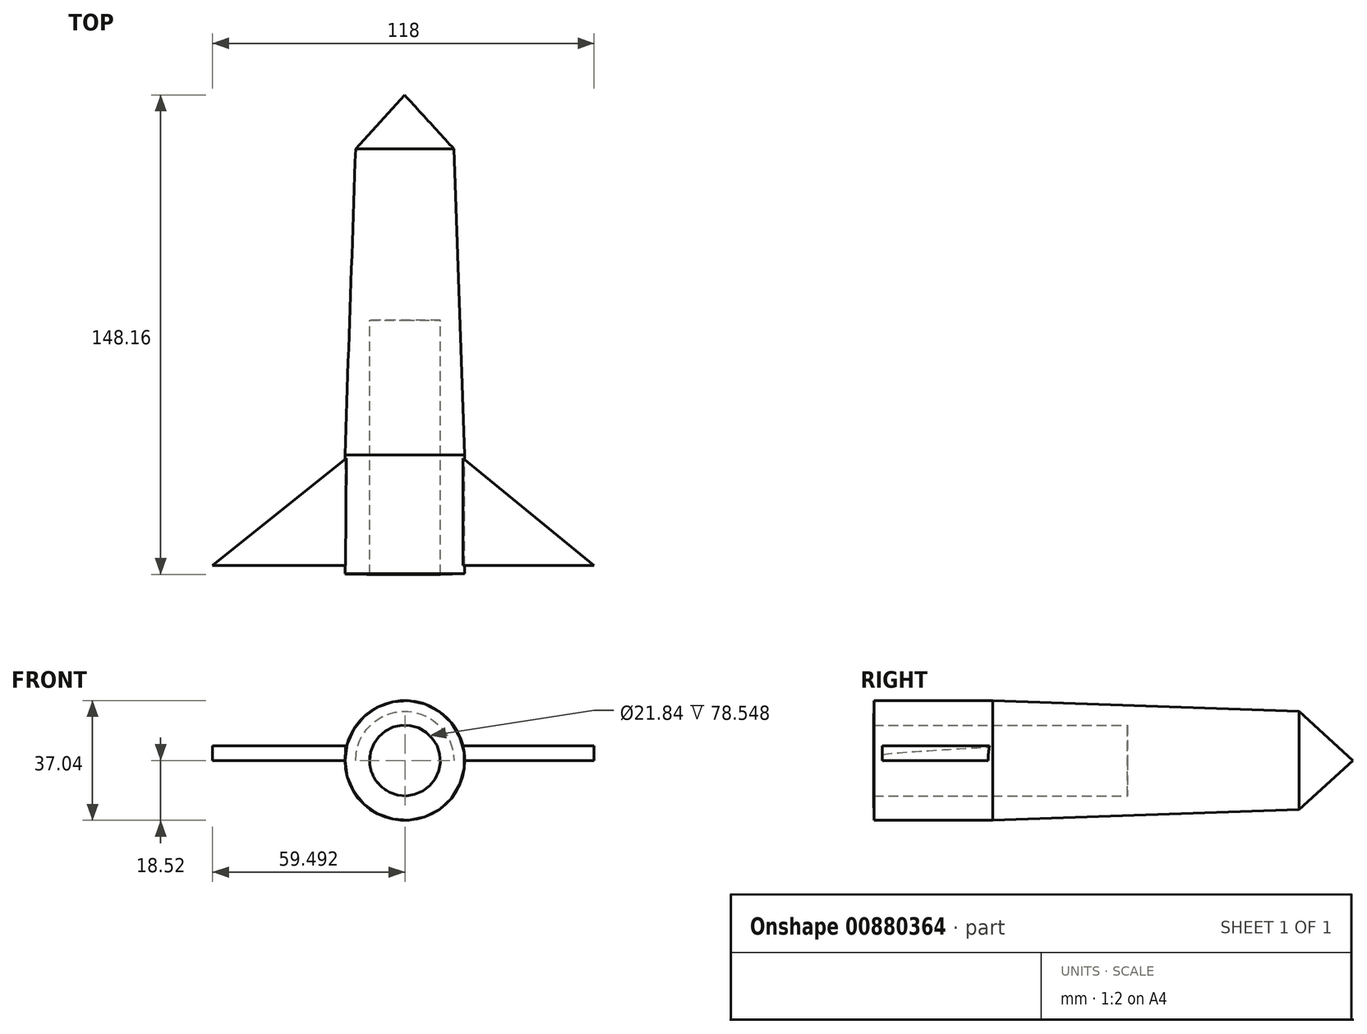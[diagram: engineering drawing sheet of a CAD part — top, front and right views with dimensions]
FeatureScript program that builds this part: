
annotation { "Feature Type Name" : "Feature", "Feature Type Description" : "" }
export const myFeature = defineFeature(function(context is Context, id is Id, definition is map)
    precondition{}
    {
        {
            var Q0;
            Q0=qCreatedBy(makeId("Top.planeOp"),FACE);
            var sketch = newSketch(context, id + "F0", { "sketchPlane" : qUnion([Q0])});
            skLineSegment(sketch, "E0", {"start": v(-34.42, 69.61) * mm, "end": v(-19.22, 52.98) * mm});
            skLineSegment(sketch, "E1", {"start": v(-19.22, 52.98) * mm, "end": v(-15.86, -41.65) * mm});
            skPoint(sketch, "E2.end.orphan", {"position": v(19.13, -78.96) * mm});
            skLineSegment(sketch, "E3", {"start": v(-15.86, -41.65) * mm, "end": v(-15.86, -78.39) * mm});
            skLineSegment(sketch, "E4", {"start": v(-34.36, -78.75) * mm, "end": v(-15.86, -78.39) * mm});
            skPoint(sketch, "E5.end.orphan", {"position": v(-34.42, -78.96) * mm});
            skLineSegment(sketch, "E6", {"start": v(-34.42, 69.61) * mm, "end": v(-34.36, -78.75) * mm});
            skSolve(sketch);
        }
        {
            var Q0;
            Q0=makeQuery(id+"F0.imprint","IMPRINT",FACE,{"disambiguationData":[TD([[makeQuery(id+"F0.imprint","IMPRINT",EDGE,{"derivedFrom":sQuery(id+"F0.wireOp",EDGE,"E0")}),-1.0]])]});
            var Q1;
            Q1=sQuery(id+"F0.wireOp",EDGE,"E6");
            revolve(context, id + "F1", {"surfaceOperationType" : NewSurfaceOperationType.NEW, "entities" : qUnion([Q0]), "axis" : qUnion([Q1]), "revolveType" : RevolveType.FULL});
        }
        {
            var Q0;
            Q0=qCreatedBy(makeId("Top.planeOp"),FACE);
            var sketch = newSketch(context, id + "F2", { "sketchPlane" : qUnion([Q0])});
            skLineSegment(sketch, "E7", {"start": v(-16.91, -42.28) * mm, "end": v(24.16, -75.86) * mm});
            skLineSegment(sketch, "E8", {"start": v(24.16, -75.86) * mm, "end": v(-16.91, -75.86) * mm});
            skPoint(sketch, "E9.MirrorCS.end.orphan", {"position": v(16, -35.6) * mm});
            skPoint(sketch, "E9.MirrorCS.start.orphan", {"position": v(24.16, -75.86) * mm});
            skLineSegment(sketch, "E10", {"start": v(-52.44, -42.68) * mm, "end": v(-93.84, -75.86) * mm});
            skLineSegment(sketch, "E11", {"start": v(246.14, -75.28) * mm, "end": v(287.2, -75.86) * mm});
            skLineSegment(sketch, "E12", {"start": v(-93.84, -75.86) * mm, "end": v(-52.77, -75.86) * mm});
            skLineSegment(sketch, "E13", {"start": v(-52.77, -75.86) * mm, "end": v(-52.44, -42.68) * mm});
            skLineSegment(sketch, "E14", {"start": v(-16.91, -42.28) * mm, "end": v(-16.91, -75.86) * mm});
            skSolve(sketch);
        }
        {
            var Q0;
            Q0=makeQuery(id+"F2.imprint","IMPRINT",FACE,{"disambiguationData":[TD([[makeQuery(id+"F2.imprint","IMPRINT",EDGE,{"derivedFrom":sQuery(id+"F2.wireOp",EDGE,"E10")}),1.0]])]});
            var Q1;
            Q1=makeQuery(id+"F2.imprint","IMPRINT",FACE,{"disambiguationData":[TD([[makeQuery(id+"F2.imprint","IMPRINT",EDGE,{"derivedFrom":sQuery(id+"F2.wireOp",EDGE,"E7")}),-1.0]])]});
            extrude(context, id + "F3", {"entities" : qUnion([Q0, Q1]), "operationType" : NewBodyOperationType.ADD, "depth" : 4.57 * mm, "offsetDistance" : 25.4 * mm});
        }
        {
            var Q0;
            Q0=qCreatedBy(makeId("Front.planeOp"),FACE);
            var sketch = newSketch(context, id + "F4", { "sketchPlane" : qUnion([Q0])});
            skPoint(sketch, "E15.center.orphan", {"position": v(-128.3, 0) * mm});
            skCircle(sketch, "E16", {"center": v(-34.35, 0) * mm, "radius": 10.92 * mm});
            skSolve(sketch);
        }
        {
            var Q0;
            Q0 = qSketchRegion(id + "F4", true);
            extrude(context, id + "F5", {"entities" : qUnion([Q0]), "operationType" : NewBodyOperationType.REMOVE, "depth" : 88.4 * mm, "offsetDistance" : 25.4 * mm});
        }
    });
